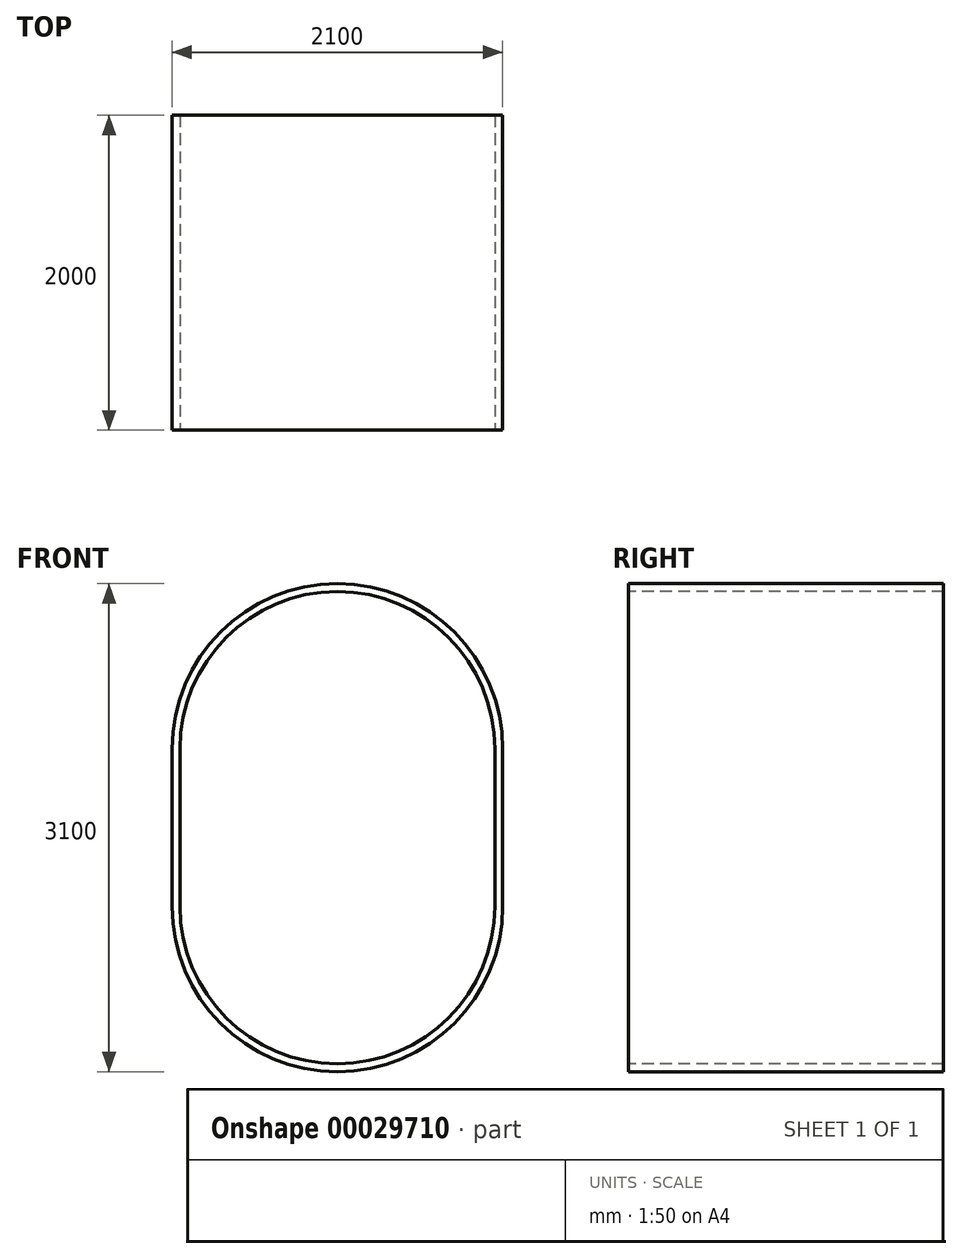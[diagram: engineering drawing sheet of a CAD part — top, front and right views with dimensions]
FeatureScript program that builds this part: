
annotation { "Feature Type Name" : "Feature", "Feature Type Description" : "" }
export const myFeature = defineFeature(function(context is Context, id is Id, definition is map)
    precondition{}
    {
        {
            var Q0;
            Q0=qCreatedBy(makeId("Front.planeOp"),FACE);
            var sketch = newSketch(context, id + "F0", { "sketchPlane" : qUnion([Q0])});
            skLineSegment(sketch, "E0.bottom", {"start": v(-689.83, 3000) * mm, "end": v(-689.83, 3000) * mm});
            skLineSegment(sketch, "E0.top", {"start": v(-689.83, 0) * mm, "end": v(-689.83, 0) * mm});
            skLineSegment(sketch, "E0.left", {"start": v(-1689.83, 2000) * mm, "end": v(-1689.83, 1000) * mm});
            skLineSegment(sketch, "E0.right", {"start": v(310.17, 2000) * mm, "end": v(310.17, 1000) * mm});
            skPoint(sketch, "E1.visualSharp", {"position": v(-1689.83, 3000) * mm});
            skArc(sketch, "E1.filletArc", {"start": v(-689.83, 3000) * mm, "mid": v(-1396.94, 2707.1) * mm, "end": v(-1689.83, 2000) * mm});
            skPoint(sketch, "E2.visualSharp", {"position": v(310.17, 3000) * mm});
            skArc(sketch, "E2.filletArc", {"start": v(310.17, 2000) * mm, "mid": v(17.27, 2707.1) * mm, "end": v(-689.83, 3000) * mm});
            skPoint(sketch, "E3.visualSharp", {"position": v(-1689.83, 0) * mm});
            skArc(sketch, "E3.filletArc", {"start": v(-1689.83, 1000) * mm, "mid": v(-1396.94, 292.9) * mm, "end": v(-689.83, 0) * mm});
            skPoint(sketch, "E4.visualSharp", {"position": v(310.17, 0) * mm});
            skArc(sketch, "E4.filletArc", {"start": v(-689.83, 0) * mm, "mid": v(17.27, 292.9) * mm, "end": v(310.17, 1000) * mm});
            skArc(sketch, "E5.0", {"start": v(-689.83, 3050) * mm, "mid": v(-1432.3, 2742.46) * mm, "end": v(-1739.83, 2000) * mm});
            skArc(sketch, "E5.1", {"start": v(360.17, 2000) * mm, "mid": v(52.63, 2742.46) * mm, "end": v(-689.83, 3050) * mm});
            skLineSegment(sketch, "E5.2", {"start": v(360.17, 2000) * mm, "end": v(360.17, 1000) * mm});
            skArc(sketch, "E5.3", {"start": v(-689.83, -50) * mm, "mid": v(52.63, 257.54) * mm, "end": v(360.17, 1000) * mm});
            skArc(sketch, "E5.4", {"start": v(-1739.83, 1000) * mm, "mid": v(-1432.3, 257.54) * mm, "end": v(-689.83, -50) * mm});
            skLineSegment(sketch, "E5.5", {"start": v(-1739.83, 2000) * mm, "end": v(-1739.83, 1000) * mm});
            skSolve(sketch);
        }
        {
            var Q0;
            Q0=makeQuery(id+"F0.imprint","IMPRINT",FACE,{"disambiguationData":[TD([[makeQuery(id+"F0.imprint","IMPRINT",EDGE,{"derivedFrom":sQuery(id+"F0.wireOp",EDGE,"E0.left")}),1.0]])]});
            var Q1;
            Q1=makeQuery(id+"F0.imprint","IMPRINT",FACE,{"disambiguationData":[TD([[makeQuery(id+"F0.imprint","IMPRINT",EDGE,{"derivedFrom":sQuery(id+"F0.wireOp",EDGE,"E0.left")}),-1.0]])]});
            var Q2;
            Q2=sQuery(id+"F0.wireOp",EDGE,"E5.0");
            var Q3;
            Q3=sQuery(id+"F0.wireOp",EDGE,"E1.filletArc");
            var Q4;
            Q4=sQuery(id+"F0.wireOp",EDGE,"E2.filletArc");
            var Q5;
            Q5=sQuery(id+"F0.wireOp",EDGE,"E5.1");
            var Q6;
            Q6=sQuery(id+"F0.wireOp",EDGE,"E5.2");
            var Q7;
            Q7=sQuery(id+"F0.wireOp",EDGE,"E0.right");
            var Q8;
            Q8=sQuery(id+"F0.wireOp",EDGE,"E4.filletArc");
            var Q9;
            Q9=sQuery(id+"F0.wireOp",EDGE,"E5.3");
            var Q10;
            Q10=sQuery(id+"F0.wireOp",EDGE,"E5.4");
            var Q11;
            Q11=sQuery(id+"F0.wireOp",EDGE,"E3.filletArc");
            var Q12;
            Q12=sQuery(id+"F0.wireOp",EDGE,"E0.left");
            var Q13;
            Q13=sQuery(id+"F0.wireOp",EDGE,"E5.5");
            extrude(context, id + "F1", {"entities" : qUnion([Q0, Q1]), "bodyType" : ToolBodyType.SURFACE, "surfaceEntities" : qUnion([Q2, Q3, Q4, Q5, Q6, Q7, Q8, Q9, Q10, Q11, Q12, Q13]), "depth" : 2000 * mm});
        }
    });
